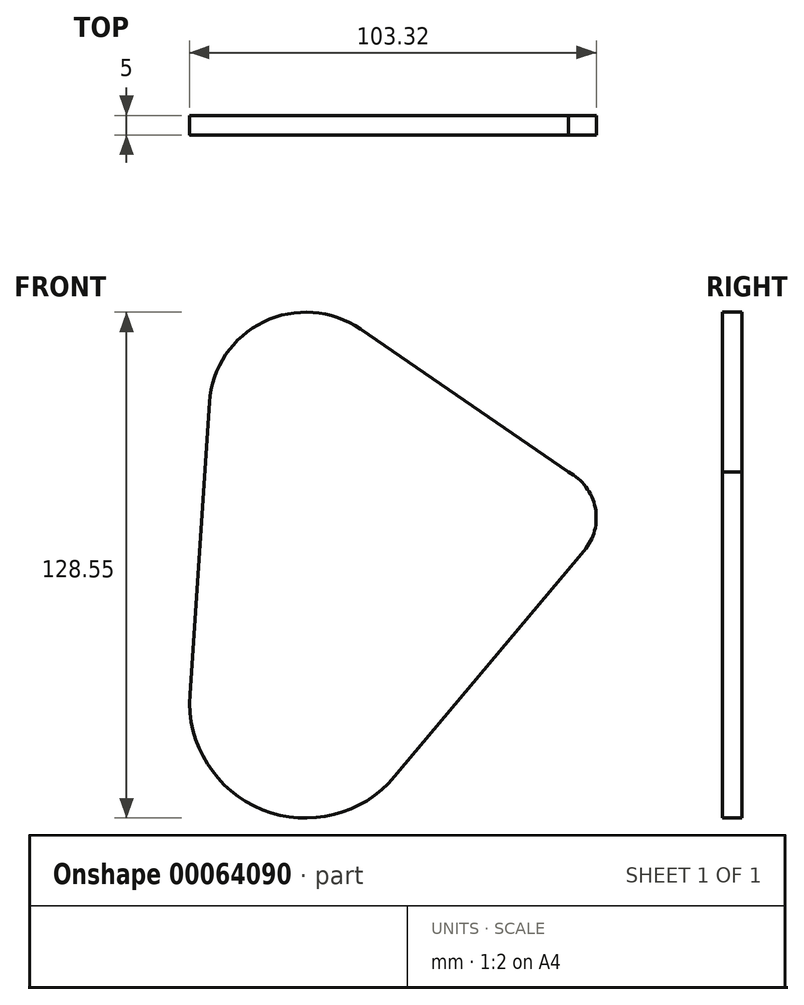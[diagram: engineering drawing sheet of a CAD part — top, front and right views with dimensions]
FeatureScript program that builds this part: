
annotation { "Feature Type Name" : "Feature", "Feature Type Description" : "" }
export const myFeature = defineFeature(function(context is Context, id is Id, definition is map)
    precondition{}
    {
        {
            var Q0;
            Q0=qCreatedBy(makeId("Front.planeOp"),FACE);
            var sketch = newSketch(context, id + "F0", { "sketchPlane" : qUnion([Q0])});
            skArc(sketch, "E0", {"start": v(-29.44, 1.97) * mm, "mid": v(-11.01, -27.38) * mm, "end": v(22.6, -18.97) * mm});
            skArc(sketch, "E1", {"start": v(13.88, 94.73) * mm, "mid": v(-10.69, 96.58) * mm, "end": v(-24.47, 76.15) * mm});
            skArc(sketch, "E2", {"start": v(70.75, 38.41) * mm, "mid": v(73.56, 49.35) * mm, "end": v(66.8, 58.4) * mm});
            skLineSegment(sketch, "E3", {"start": v(70.75, 38.41) * mm, "end": v(22.6, -18.97) * mm});
            skLineSegment(sketch, "E4", {"start": v(-24.47, 76.15) * mm, "end": v(-29.44, 1.97) * mm});
            skLineSegment(sketch, "E5", {"start": v(66.8, 58.4) * mm, "end": v(13.88, 94.73) * mm});
            skLineSegment(sketch, "E6.0", {"start": v(68.83, 40.02) * mm, "end": v(20.69, -17.36) * mm});
            skArc(sketch, "E7.0", {"start": v(-26.95, 1.8) * mm, "mid": v(-10.08, -25.06) * mm, "end": v(20.69, -17.36) * mm});
            skLineSegment(sketch, "E8.0", {"start": v(-21.97, 75.99) * mm, "end": v(-26.95, 1.8) * mm});
            skArc(sketch, "E9.0", {"start": v(12.47, 92.67) * mm, "mid": v(-9.6, 94.33) * mm, "end": v(-21.97, 75.99) * mm});
            skLineSegment(sketch, "E10.0", {"start": v(65.38, 56.33) * mm, "end": v(12.47, 92.67) * mm});
            skArc(sketch, "E11.0", {"start": v(68.83, 40.02) * mm, "mid": v(71.1, 48.86) * mm, "end": v(65.63, 56.18) * mm});
            skSolve(sketch);
        }
        {
            var Q0;
            Q0=makeQuery(id+"F0.imprint","IMPRINT",FACE,{"disambiguationData":[TD([[makeQuery(id+"F0.imprint","IMPRINT",EDGE,{"derivedFrom":sQuery(id+"F0.wireOp",EDGE,"E0")}),1.0]])]});
            extrude(context, id + "F1", {"entities" : qUnion([Q0]), "depth" : 5 * mm});
        }
    });
